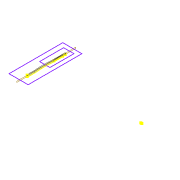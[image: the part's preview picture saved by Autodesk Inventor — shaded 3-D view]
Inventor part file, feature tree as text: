
AUTODESK INVENTOR PART (.ipt)
format: ipt  version: 2022 (Build 260153000, 153)  size: 120,832 bytes
history: native  units: mm
features: sketch x3, extrude x1, projected_geometry x1
ambient origin geometry x8: Origin, YZ Plane, XZ Plane, XY Plane, X Axis, Y Axis, Z Axis, Center Point
bodies: Solid1 (feature_tree)
feature tree (5):
  extrude  "Extrusion1"  Depth=8.0mm
  sketch  "Sketch2"  dims[d2=3.0mm]
  sketch  "Sketch3"  dims[d3=3.0mm d4=8.0mm d5=0.0mm d10=3.0mm d11=19.5mm d12=80.0mm d13=85.0mm d14=220.0mm d15=700.0mm d16=700.0mm]
  sketch  "Sketch1"  dims[d0=270.69mm d1=8.0mm]
  projected_geometry  "Projected Loop1"
